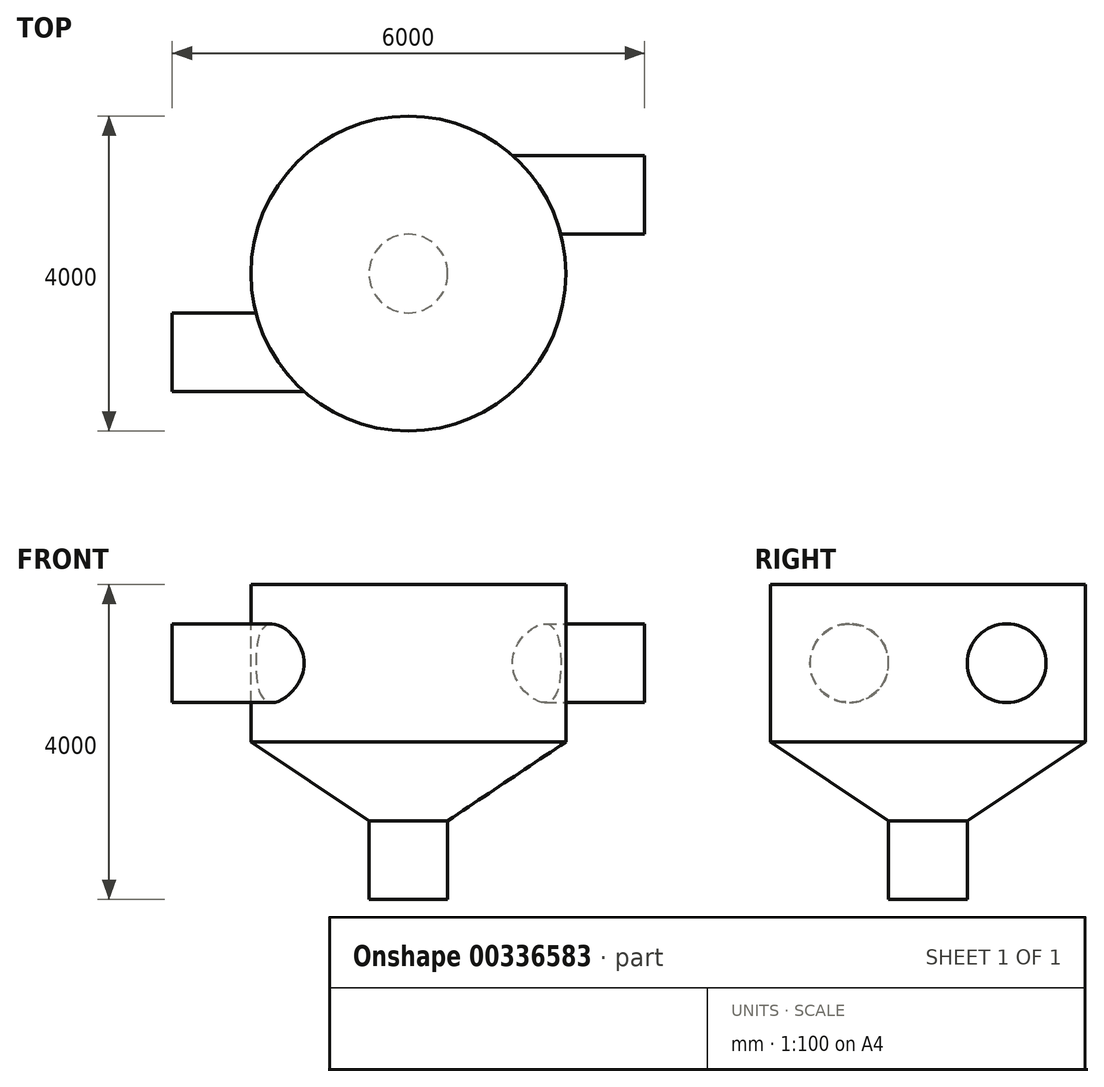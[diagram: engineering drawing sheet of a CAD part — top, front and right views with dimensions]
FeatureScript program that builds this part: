
annotation { "Feature Type Name" : "Feature", "Feature Type Description" : "" }
export const myFeature = defineFeature(function(context is Context, id is Id, definition is map)
    precondition{}
    {
        {
            var Q0;
            Q0=qCreatedBy(makeId("Front.planeOp"),FACE);
            var sketch = newSketch(context, id + "F0", { "sketchPlane" : qUnion([Q0])});
            skLineSegment(sketch, "E0", {"start": v(0, 0) * mm, "end": v(500, 0) * mm});
            skLineSegment(sketch, "E1", {"start": v(500, 0) * mm, "end": v(500, 1000) * mm});
            skLineSegment(sketch, "E2", {"start": v(0, 0) * mm, "end": v(2000, 0) * mm, "construction": true});
            skLineSegment(sketch, "E3", {"start": v(2000, 0) * mm, "end": v(2000, 2000) * mm, "construction": true});
            skLineSegment(sketch, "E4", {"start": v(500, 1000) * mm, "end": v(2000, 2000) * mm});
            skLineSegment(sketch, "E5", {"start": v(2000, 2000) * mm, "end": v(2000, 4000) * mm});
            skLineSegment(sketch, "E6", {"start": v(2000, 4000) * mm, "end": v(0, 4000) * mm});
            skLineSegment(sketch, "E7", {"start": v(0, 4000) * mm, "end": v(0, 0) * mm});
            skSolve(sketch);
        }
        {
            var Q0;
            Q0 = qSketchRegion(id + "F0", true);
            var Q1;
            Q1=sQuery(id+"F0.wireOp",EDGE,"E7");
            revolve(context, id + "F1", {"entities" : qUnion([Q0]), "axis" : qUnion([Q1]), "revolveType" : RevolveType.FULL});
        }
        {
            var Q0;
            Q0=qCreatedBy(makeId("Right.planeOp"),FACE);
            cPlane(context, id + "F2", {"entities" : qUnion([Q0]), "cplaneType" : CPlaneType.OFFSET, "offset" : 3000 * mm, "width" : 150 * mm, "height" : 150 * mm});
        }
        {
            var Q0;
            Q0=qCreatedBy(id+"F2.planeOp",FACE);
            var sketch = newSketch(context, id + "F3", { "sketchPlane" : qUnion([Q0])});
            skLineSegment(sketch, "E8", {"start": v(0, 0) * mm, "end": v(1000, 0) * mm, "construction": true});
            skLineSegment(sketch, "E9", {"start": v(1000, 0) * mm, "end": v(1000, 3000) * mm, "construction": true});
            skCircle(sketch, "E10", {"center": v(1000, 3000) * mm, "radius": 500 * mm});
            skSolve(sketch);
        }
        {
            var Q0;
            Q0=qCreatedBy(makeId("Right.planeOp"),FACE);
            cPlane(context, id + "F4", {"entities" : qUnion([Q0]), "cplaneType" : CPlaneType.OFFSET, "offset" : 3000 * mm, "oppositeDirection" : true, "width" : 150 * mm, "height" : 150 * mm});
        }
        {
            var Q0;
            Q0=qCreatedBy(id+"F4.planeOp",FACE);
            var sketch = newSketch(context, id + "F5", { "sketchPlane" : qUnion([Q0])});
            skLineSegment(sketch, "E11", {"start": v(0, 0) * mm, "end": v(-1000, 0) * mm, "construction": true});
            skLineSegment(sketch, "E12", {"start": v(-1000, 0) * mm, "end": v(-1000, 3000) * mm, "construction": true});
            skCircle(sketch, "E13", {"center": v(-1000, 3000) * mm, "radius": 500 * mm});
            skSolve(sketch);
        }
        {
            var Q0;
            Q0 = qSketchRegion(id + "F3", true);
            extrude(context, id + "F6", {"entities" : qUnion([Q0]), "endBound" : BoundingType.UP_TO_NEXT, "oppositeDirection" : true, "depth" : 25 * mm});
        }
        {
            var Q0;
            Q0 = qSketchRegion(id + "F5", true);
            extrude(context, id + "F7", {"entities" : qUnion([Q0]), "operationType" : NewBodyOperationType.ADD, "endBound" : BoundingType.UP_TO_NEXT, "depth" : 25 * mm});
        }
    });
